# Revit family: Sanitary_Toilet-Cisterns_Sanindusa_Sanfix-Metal-Support-for-Wall-Mounted-WC
name_source: partatom
category: Plumbing Fixtures
revit_build: Autodesk Revit 2018 (Build: 20170223_1515(x64)
units: mm (PartAtom-declared; Revit-internal decimal feet)

## family parameters
Always vertical = Yes
Cut with Voids When Loaded = No
Host = Wall
OmniClass Number = 23.45.00.00
OmniClass Title = Sanitary, Laundry, and Cleaning Equipment
Part Type = Normal
Room Calculation Point = No
Round Connector Dimension = Use Diameter
Shared = No

## types (1)
- Sanindusa
    AssetType = Fixed
    CisternCapacity = 7.5 Lts
    CisternColor = white
    CisternHeight = HighLevel
    CisternMaterial = PE-HD
    CodePerformance = EN 14124:2004 | EN 14055:2010 CL 1 - 7 - NL II
    Constituents = General content (material included):
Supporting frame for mounting; Height adjustable galvanized support legs; Depth adjustable galvanised brackets for pre-wall installation; Universal connection to water DN 15 (1/2") with a built-in angle valve; PE wall drain elbow ø 90/90 mm with seal; PE adapter reduction piece ø 90/110 mm with seal; Depth adjustable drain elbow (+/– 10 mm); Connecting parts for mounting toilet bowls; Other parts necessary to fix and connect the product; Structure assembly instructions; Installation instructions for the toilet. 
Compatible plates (not included): 40003 - Orange 3|6L mechanism plate, 40013 - Plan 3|6L mechanism plate, 40023 - Easy 3|6L mechanism plate, 40033 - Moon 3|6L mechanism plate, 40043 - Square mechanism plate.
    Cost = 0 $
    Description = Metal support sanfix for wall mounted WC with cistern and 3|6L mechanism
    Edition number = 1
    Element Type = CISTERN: A water storage unit attached to a sanitary terminal that is fitted with a device, operated automatically or by the user, that discharges water to cleanse a water closet (toilet) pan, urinal or slop hopper. (BS6100 330 5008)
    Features = Supporting frame for wall-mounted toilets with a concealed flushing cistern. For frontal activation. Used for mounting a dual flush flushing plate. The flushing cistern is insulated against condensation. Silent filling valve. Connection to water: at the top left/middle/right and from the right side. Support legs equipped with a brake for easier installation – ranging from 0 to 24 cm. Range of brackets for pre-wall installation: from 12 to 20 cm. Suitable for the installation of toilet bowls with an axial distance of 18 or 23 cm.
    Finish = blue powder coating
    FlushRate = Lowerbound:3/4Lts
Upperbound:5/6/7Lts
    FlushType = push
    Installation Instructions = https://www.tec.sanindusa.pt
    IsAutomaticFlush = FALSE
    IsSingleFlush = FALSE
    Manufacturer = www.sanindusa.pt
    ManufacturerName = Sanindusa
    ManufacturerURL = www.tec.sanindusa.pt
    Material = blue powder coating
    ModelNumber = 40333
    ModelReference = Sanfix
    Name = Metal support sanfix for wall mounted WC
    NominalHeight = 1150 mm
    NominalLength = 500 mm
    NominalWidth = 120 mm
    Pre-defined type (IFC) = CISTERN
    Product Guid = ef304a7c-3bd0-4582-b0e5-10f5c8d4fd32
    Product data url = https://bimobject.com
    ProductInformation = https://www.tec.sanindusa.pt
    Size = 50x20x115
    Type (IFC) = IfcSanitaryTerminalType
    URL = www.tec.sanindusa.pt
    Uniclass2015Code = Pr_40_20_93_89
    Uniclass2015Title = WC cisterns
    Uniclass2015Version = Products v1.6
    Version = 2
    WarrantyDescription = https://www.tec.sanindusa.pt
    WarrantyDurationParts = 5
    WarrantyDurationUnit = year
    WarrantyStartDate = 1900-12-31T23:59:59
    Weight = 13.60 kg
    X = 355 mm

## geometry (parser evidence)
native form markers: Sweep x7
no freeform markers — native parametric forms only
